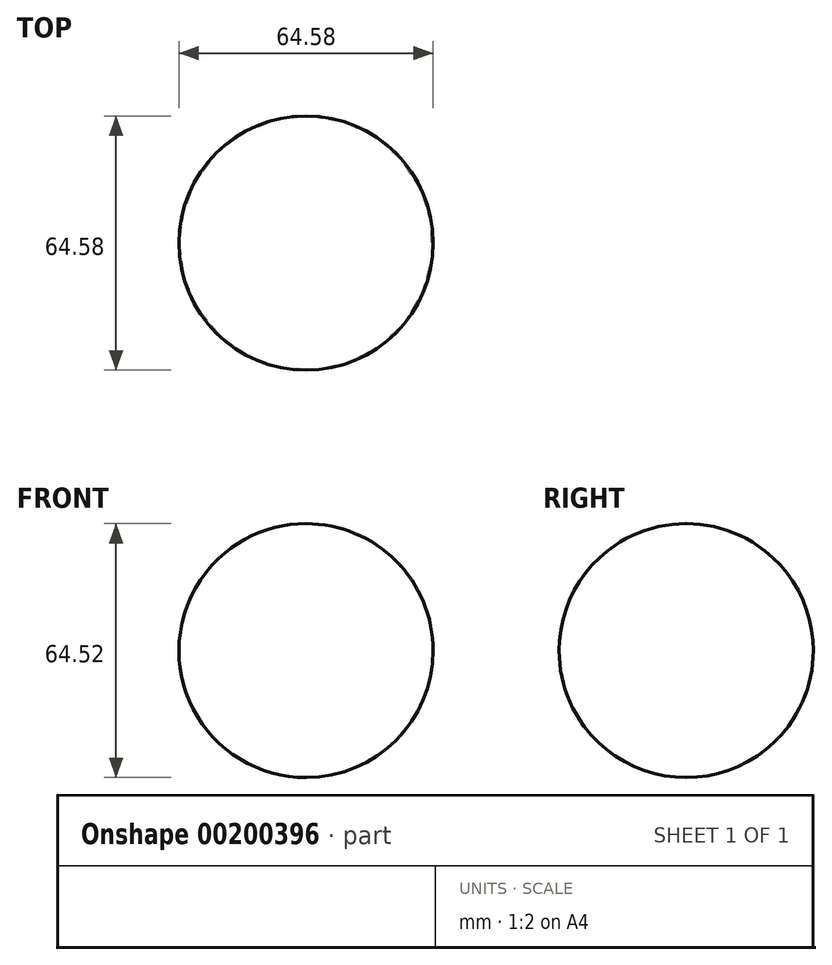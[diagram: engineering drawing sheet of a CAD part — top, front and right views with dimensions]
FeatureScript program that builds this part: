
annotation { "Feature Type Name" : "Feature", "Feature Type Description" : "" }
export const myFeature = defineFeature(function(context is Context, id is Id, definition is map)
    precondition{}
    {
        {
            var Q0;
            Q0=qCreatedBy(makeId("Front.planeOp"),FACE);
            var sketch = newSketch(context, id + "F0", { "sketchPlane" : qUnion([Q0])});
            skArc(sketch, "E0", {"start": v(-26.79, 10.8) * mm, "mid": v(5.44, 43.06) * mm, "end": v(-26.79, 75.32) * mm});
            skLineSegment(sketch, "E1", {"start": v(-26.79, 75.32) * mm, "end": v(-26.79, 10.8) * mm});
            skSolve(sketch);
        }
        {
            var Q0;
            Q0 = qSketchRegion(id + "F0", true);
            var Q1;
            Q1=sQuery(id+"F0.wireOp",EDGE,"E1");
            revolve(context, id + "F1", {"entities" : qUnion([Q0]), "axis" : qUnion([Q1]), "revolveType" : RevolveType.FULL});
        }
    });
